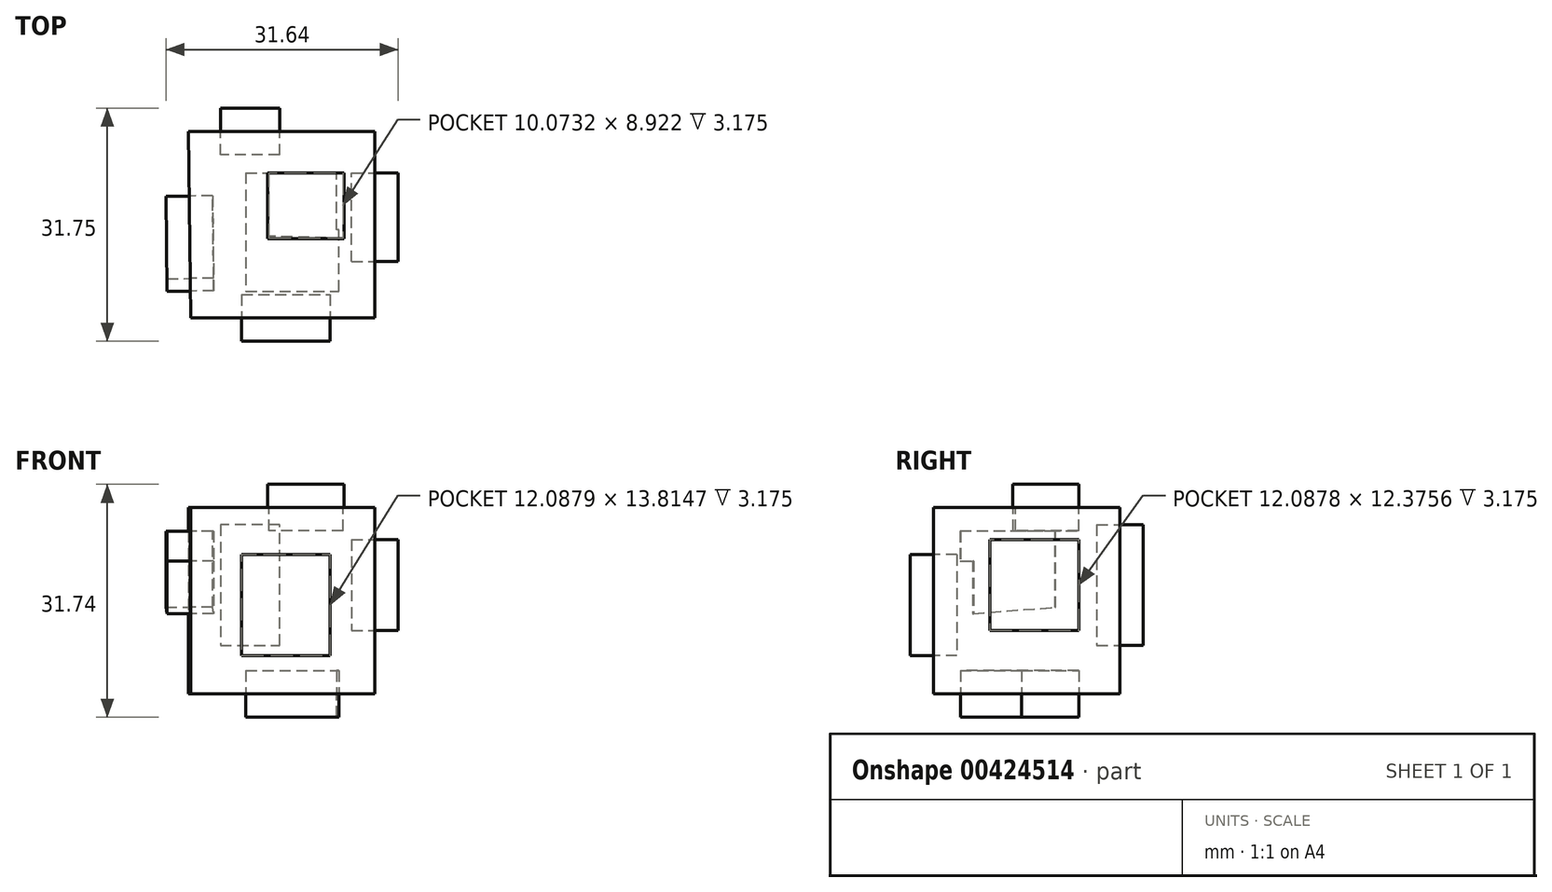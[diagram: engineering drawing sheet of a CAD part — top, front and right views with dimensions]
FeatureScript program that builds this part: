
annotation { "Feature Type Name" : "Feature", "Feature Type Description" : "" }
export const myFeature = defineFeature(function(context is Context, id is Id, definition is map)
    precondition{}
    {
        {
            var Q0;
            Q0=qCreatedBy(makeId("Top.planeOp"),FACE);
            var sketch = newSketch(context, id + "F0", { "sketchPlane" : qUnion([Q0])});
            skLineSegment(sketch, "E0", {"start": v(-16.15, 5.63) * mm, "end": v(9.25, 5.63) * mm});
            skLineSegment(sketch, "E1", {"start": v(-15.84, -19.77) * mm, "end": v(9.25, -19.77) * mm});
            skLineSegment(sketch, "E2", {"start": v(-15.84, -19.77) * mm, "end": v(-16.15, 5.63) * mm});
            skLineSegment(sketch, "E3", {"start": v(9.25, -19.77) * mm, "end": v(9.25, 5.63) * mm});
            skSolve(sketch);
        }
        {
            var Q0;
            Q0 = qSketchRegion(id + "F0", true);
            extrude(context, id + "F1", {"entities" : qUnion([Q0]), "depth" : 25.4 * mm});
        }
        {
            var Q0;
            Q0=makeQuery(id+"F1.opExtrude","CAP_FACE",FACE,{"disambiguationData":[OSD([sQuery(id+"F0.wireOp",EDGE,"E0"),sQuery(id+"F0.wireOp",EDGE,"E1"),sQuery(id+"F0.wireOp",EDGE,"E2"),sQuery(id+"F0.wireOp",EDGE,"E3")])],"isStart":false});
            var sketch = newSketch(context, id + "F2", { "sketchPlane" : qUnion([Q0])});
            skLineSegment(sketch, "E4", {"start": v(-5.18, -8.63) * mm, "end": v(-5.18, 0) * mm});
            skLineSegment(sketch, "E5", {"start": v(-5.18, 0) * mm, "end": v(4.9, 0) * mm});
            skLineSegment(sketch, "E6", {"start": v(4.9, 0) * mm, "end": v(4.9, -8.92) * mm});
            skLineSegment(sketch, "E7", {"start": v(4.9, -8.92) * mm, "end": v(-5.18, -8.63) * mm});
            skSolve(sketch);
        }
        {
            var Q0;
            Q0=makeQuery(id+"F2.imprint","IMPRINT",FACE,{"disambiguationData":[TD([[makeQuery(id+"F2.imprint","IMPRINT",EDGE,{"derivedFrom":makeQuery(id+"F1.opExtrude","CAP_EDGE",EDGE,{"disambiguationData":[OSD([sQuery(id+"F0.wireOp",EDGE,"E0")])],"isStart":false})}),-1.0]])]});
            var sketch = newSketch(context, id + "F3", { "sketchPlane" : qUnion([Q0])});
            skSolve(sketch);
        }
        {
            var Q0;
            Q0 = qSketchRegion(id + "F2", true);
            extrude(context, id + "F4", {"entities" : qUnion([Q0]), "operationType" : NewBodyOperationType.REMOVE, "oppositeDirection" : true, "depth" : 3.17 * mm});
        }
        {
            var Q0;
            Q0=makeQuery(id+"F1.opExtrude","SWEPT_FACE",FACE,{"disambiguationData":[OSD([sQuery(id+"F0.wireOp",EDGE,"E3")])]});
            var sketch = newSketch(context, id + "F5", { "sketchPlane" : qUnion([Q0])});
            skLineSegment(sketch, "E8", {"start": v(-12.09, 16.4) * mm, "end": v(0, 16.4) * mm});
            skLineSegment(sketch, "E9", {"start": v(0, 16.4) * mm, "end": v(0, 8.63) * mm});
            skLineSegment(sketch, "E10", {"start": v(0, 8.63) * mm, "end": v(-12.09, 8.63) * mm});
            skLineSegment(sketch, "E11", {"start": v(-12.09, 8.63) * mm, "end": v(-12.09, 16.4) * mm});
            skPoint(sketch, "E12.oppositeSnap0", {"position": v(-12.09, 12.52) * mm});
            skLineSegment(sketch, "E12.bottom", {"start": v(-6.04, 16.4) * mm, "end": v(-12.09, 16.4) * mm});
            skLineSegment(sketch, "E12.top", {"start": v(-6.04, 21) * mm, "end": v(-12.09, 21) * mm});
            skLineSegment(sketch, "E12.left", {"start": v(-6.04, 16.4) * mm, "end": v(-6.04, 21) * mm});
            skLineSegment(sketch, "E12.right", {"start": v(-12.09, 16.4) * mm, "end": v(-12.09, 21) * mm});
            skLineSegment(sketch, "E13.bottom", {"start": v(-6.04, 21) * mm, "end": v(0, 21) * mm});
            skLineSegment(sketch, "E13.top", {"start": v(-6.04, 21) * mm, "end": v(0, 21) * mm});
            skLineSegment(sketch, "E13.left", {"start": v(-6.04, 21) * mm, "end": v(-6.04, 21) * mm});
            skLineSegment(sketch, "E13.right", {"start": v(0, 21) * mm, "end": v(0, 21) * mm});
            skLineSegment(sketch, "E14.top", {"start": v(0, 16.4) * mm, "end": v(0, 16.4) * mm});
            skLineSegment(sketch, "E14.left", {"start": v(0, 21) * mm, "end": v(0, 16.4) * mm});
            skLineSegment(sketch, "E14.right", {"start": v(0, 21) * mm, "end": v(0, 16.4) * mm});
            skSolve(sketch);
        }
        {
            var Q0;
            Q0 = qSketchRegion(id + "F5", true);
            extrude(context, id + "F6", {"entities" : qUnion([Q0]), "operationType" : NewBodyOperationType.REMOVE, "oppositeDirection" : true, "depth" : 3.17 * mm});
        }
        {
            var Q0;
            Q0=makeQuery(id+"F1.opExtrude","SWEPT_FACE",FACE,{"disambiguationData":[OSD([sQuery(id+"F0.wireOp",EDGE,"E0")])]});
            var sketch = newSketch(context, id + "F7", { "sketchPlane" : qUnion([Q0])});
            skLineSegment(sketch, "E15", {"start": v(3.74, 15.83) * mm, "end": v(11.8, 15.83) * mm});
            skLineSegment(sketch, "E16", {"start": v(11.8, 15.83) * mm, "end": v(11.8, 6.62) * mm});
            skLineSegment(sketch, "E17", {"start": v(11.8, 6.62) * mm, "end": v(3.74, 6.62) * mm});
            skLineSegment(sketch, "E18", {"start": v(3.74, 6.62) * mm, "end": v(3.74, 15.83) * mm});
            skLineSegment(sketch, "E19.top", {"start": v(3.74, 23.02) * mm, "end": v(11.8, 23.02) * mm});
            skLineSegment(sketch, "E19.left", {"start": v(3.74, 15.83) * mm, "end": v(3.74, 23.02) * mm});
            skLineSegment(sketch, "E19.right", {"start": v(11.8, 15.83) * mm, "end": v(11.8, 23.02) * mm});
            skSolve(sketch);
        }
        {
            var Q0;
            Q0 = qSketchRegion(id + "F7", true);
            extrude(context, id + "F8", {"entities" : qUnion([Q0]), "operationType" : NewBodyOperationType.REMOVE, "oppositeDirection" : true, "depth" : 3.17 * mm});
        }
        {
            var Q0;
            Q0=makeQuery(id+"F1.opExtrude","SWEPT_FACE",FACE,{"disambiguationData":[OSD([sQuery(id+"F0.wireOp",EDGE,"E1")])]});
            var sketch = newSketch(context, id + "F9", { "sketchPlane" : qUnion([Q0])});
            skLineSegment(sketch, "E20", {"start": v(-8.92, 13.53) * mm, "end": v(3.17, 13.53) * mm});
            skLineSegment(sketch, "E21", {"start": v(3.17, 13.53) * mm, "end": v(3.17, 5.18) * mm});
            skLineSegment(sketch, "E22", {"start": v(3.17, 5.18) * mm, "end": v(-7.2, 5.18) * mm});
            skLineSegment(sketch, "E23", {"start": v(-7.2, 5.18) * mm, "end": v(-8.92, 5.18) * mm});
            skLineSegment(sketch, "E24", {"start": v(-8.92, 5.18) * mm, "end": v(-8.92, 13.53) * mm});
            skLineSegment(sketch, "E25.top", {"start": v(-8.92, 19) * mm, "end": v(3.17, 19) * mm});
            skLineSegment(sketch, "E25.left", {"start": v(-8.92, 13.53) * mm, "end": v(-8.92, 19) * mm});
            skLineSegment(sketch, "E25.right", {"start": v(3.17, 13.53) * mm, "end": v(3.17, 19) * mm});
            skSolve(sketch);
        }
        {
            var Q0;
            Q0 = qSketchRegion(id + "F9", true);
            extrude(context, id + "F10", {"entities" : qUnion([Q0]), "operationType" : NewBodyOperationType.REMOVE, "oppositeDirection" : true, "depth" : 3.17 * mm});
        }
        {
            var Q0;
            Q0=makeQuery(id+"F1.opExtrude","SWEPT_FACE",FACE,{"disambiguationData":[OSD([sQuery(id+"F0.wireOp",EDGE,"E2")])]});
            var sketch = newSketch(context, id + "F11", { "sketchPlane" : qUnion([Q0])});
            skLineSegment(sketch, "E26", {"start": v(2.97, 11.8) * mm, "end": v(2.97, 18.13) * mm});
            skLineSegment(sketch, "E27", {"start": v(2.97, 18.13) * mm, "end": v(14.2, 18.13) * mm});
            skLineSegment(sketch, "E28", {"start": v(14.2, 18.13) * mm, "end": v(14.2, 10.94) * mm});
            skLineSegment(sketch, "E29", {"start": v(14.2, 10.94) * mm, "end": v(2.97, 11.8) * mm});
            skLineSegment(sketch, "E30.bottom", {"start": v(8.58, 18.13) * mm, "end": v(2.97, 18.13) * mm});
            skLineSegment(sketch, "E30.top", {"start": v(8.58, 22.16) * mm, "end": v(2.97, 22.16) * mm});
            skLineSegment(sketch, "E30.left", {"start": v(8.58, 18.13) * mm, "end": v(8.58, 22.16) * mm});
            skLineSegment(sketch, "E30.right", {"start": v(2.97, 18.13) * mm, "end": v(2.97, 22.16) * mm});
            skLineSegment(sketch, "E31.bottom", {"start": v(8.58, 22.16) * mm, "end": v(15.92, 22.16) * mm});
            skLineSegment(sketch, "E31.top", {"start": v(8.58, 22.16) * mm, "end": v(15.92, 22.16) * mm});
            skLineSegment(sketch, "E31.left", {"start": v(8.58, 22.16) * mm, "end": v(8.58, 22.16) * mm});
            skLineSegment(sketch, "E31.right", {"start": v(15.92, 22.16) * mm, "end": v(15.92, 22.16) * mm});
            skLineSegment(sketch, "E32.bottom", {"start": v(15.92, 22.16) * mm, "end": v(14.2, 22.16) * mm});
            skLineSegment(sketch, "E32.top", {"start": v(15.92, 18.13) * mm, "end": v(14.2, 18.13) * mm});
            skLineSegment(sketch, "E32.left", {"start": v(15.92, 22.16) * mm, "end": v(15.92, 18.13) * mm});
            skLineSegment(sketch, "E32.right", {"start": v(14.2, 22.16) * mm, "end": v(14.2, 18.13) * mm});
            skSolve(sketch);
        }
        {
            var Q0;
            Q0 = qSketchRegion(id + "F11", true);
            extrude(context, id + "F12", {"entities" : qUnion([Q0]), "operationType" : NewBodyOperationType.REMOVE, "oppositeDirection" : true, "depth" : 3.17 * mm});
        }
        {
            var Q0;
            Q0=makeQuery(id+"F1.opExtrude","CAP_FACE",FACE,{"disambiguationData":[OSD([sQuery(id+"F0.wireOp",EDGE,"E0"),sQuery(id+"F0.wireOp",EDGE,"E1"),sQuery(id+"F0.wireOp",EDGE,"E2"),sQuery(id+"F0.wireOp",EDGE,"E3")])],"isStart":true});
            var sketch = newSketch(context, id + "F13", { "sketchPlane" : qUnion([Q0])});
            skLineSegment(sketch, "E33", {"start": v(-8.35, 7.77) * mm, "end": v(-8.35, 16.12) * mm});
            skLineSegment(sketch, "E34", {"start": v(-8.63, 16.12) * mm, "end": v(4.32, 16.12) * mm});
            skLineSegment(sketch, "E35", {"start": v(4.32, 16.7) * mm, "end": v(4.32, 7.77) * mm});
            skLineSegment(sketch, "E36", {"start": v(4.32, 7.77) * mm, "end": v(-8.35, 7.77) * mm});
            skLineSegment(sketch, "E37.bottom", {"start": v(-8.35, 7.77) * mm, "end": v(4.03, 7.77) * mm});
            skLineSegment(sketch, "E37.top", {"start": v(-8.35, 0) * mm, "end": v(4.03, 0) * mm});
            skLineSegment(sketch, "E37.left", {"start": v(-8.35, 7.77) * mm, "end": v(-8.35, 0) * mm});
            skLineSegment(sketch, "E37.right", {"start": v(4.03, 7.77) * mm, "end": v(4.03, 0) * mm});
            skSolve(sketch);
        }
        {
            var Q0;
            Q0 = qSketchRegion(id + "F13", true);
            extrude(context, id + "F14", {"entities" : qUnion([Q0]), "operationType" : NewBodyOperationType.REMOVE, "oppositeDirection" : true, "depth" : 3.17 * mm});
        }
        {
            var Q0;
            Q0=makeQuery(id+"F3.imprint","IMPRINT",FACE,{"disambiguationData":[TD([[makeQuery(id+"F3.imprint","IMPRINT",EDGE,{"derivedFrom":makeQuery(id+"F2.imprint","IMPRINT",EDGE,{"derivedFrom":sQuery(id+"F2.wireOp",EDGE,"E4")})}),-1.0]])]});
            var sketch = newSketch(context, id + "F15", { "sketchPlane" : qUnion([Q0])});
            skLineSegment(sketch, "E38.bottom", {"start": v(-5.38, 0) * mm, "end": v(5.06, 0) * mm});
            skLineSegment(sketch, "E38.top", {"start": v(-5.38, -8.98) * mm, "end": v(5.06, -8.98) * mm});
            skLineSegment(sketch, "E38.left", {"start": v(-5.38, 0) * mm, "end": v(-5.38, -8.98) * mm});
            skLineSegment(sketch, "E38.right", {"start": v(5.06, 0) * mm, "end": v(5.06, -8.98) * mm});
            skSolve(sketch);
        }
        {
            var Q0;
            Q0 = qSketchRegion(id + "F15", true);
            extrude(context, id + "F16", {"entities" : qUnion([Q0]), "depth" : 3.17 * mm});
        }
        {
            var Q0;
            Q0 = qSketchRegion(id + "F5", true);
            extrude(context, id + "F17", {"entities" : qUnion([Q0]), "depth" : 3.17 * mm});
        }
        {
            var Q0;
            Q0 = qSketchRegion(id + "F7", true);
            extrude(context, id + "F18", {"entities" : qUnion([Q0]), "depth" : 3.17 * mm});
        }
        {
            var Q0;
            Q0 = qSketchRegion(id + "F11", true);
            extrude(context, id + "F19", {"entities" : qUnion([Q0]), "depth" : 3.17 * mm});
        }
        {
            var Q0;
            Q0 = qSketchRegion(id + "F9", true);
            extrude(context, id + "F20", {"entities" : qUnion([Q0]), "depth" : 3.17 * mm});
        }
        {
            var Q0;
            Q0 = qSketchRegion(id + "F13", true);
            extrude(context, id + "F21", {"entities" : qUnion([Q0]), "depth" : 3.17 * mm});
        }
    });
